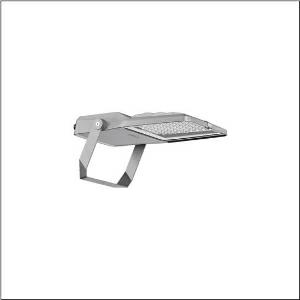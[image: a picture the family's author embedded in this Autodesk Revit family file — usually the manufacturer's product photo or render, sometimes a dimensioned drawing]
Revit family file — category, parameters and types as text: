
# Revit family: floodlight_fl_21_mini___pl61_5xa7772b1c1a_9d64
name_source: partatom
category: Lighting Fixtures
units: mm (PartAtom-declared; Revit-internal decimal feet)

## family parameters
Cut with Voids When Loaded = No
Host = Face
Light Source = No
Part Type = Normal
Room Calculation Point = No
Round Connector Dimension = Use Diameter
Shared = No

## types (1)
- --- (1 x LED, 5080 lm, 45.5 W, 2200K)
    Apparent Load = 46 VA
    CIE Flux Codes = 33 65 98 100 100
    Color Rendering = 70
    Color Temperature = 2200K
    Default Elevation = 1800 mm
    Description = Floodlight FL 21 mini, floodlight, primary light control with lens, of PMMA, primary optical cover: protective disc, of toughened safety glass, transparent, light distribution: PL61, light emission: direct distribution, installation type: surface-mounted, LED, High Power LED, rated luminous flux: 5.080lm, luminous efficacy: 112lm/W, light colour: 722, colour temperature: 2200K, control gear: ECG iQ, control: Street-Remote, Auto-Match, Temp-Guard, Night-Set, Smart-Wire, Desk-Remote (wireless, voltage-free reading and setting of iQ features in the workshop via application-optimized NFC function/RFID function), optimised constant luminous flux control (CLO 2.0), with terminal, 6-pole, mains connection: 220..240V, AC, 50/60Hz, start of lifetime: 46W, end of lifetime: 48W, reduction: 21W, luminaire housing, of diecast aluminium, powder-coated, Siteco® metallic grey (DB 702S), corrosivity category C5 according to DIN EN ISO 12944, mounting bracket, of steel, galvanised, powder-coated, Siteco® metallic grey (DB 702S), protection rating (complete): IP66, insulation class (complete): insulation class II (safety insulation), certification: CE, ENEC, VDE, protection symbol: D, impact resistance: IK08, permissible operating ambient temperature: -40..+40°C, permissible operating ambient temperature for outdoor applications: -40..+50°C, standard: DIN EN 12944, packaging unit: 1 piece

Light Distribution: PL61
    Height = 70 mm
    Lamp = 1 x LED
    Lamp Light Flux = 5080 lm
    Lamp Power = 45.5 W
    Lamp count = 1
    Length = 485 mm
    Luminous efficacy = 112 lm/W
    Manufacturer = Siteco
    ModVariant = No
    Model = 5XA7772B1C1A
    Number of Poles = 1
    OnlyDefault = Yes
    Power Factor = 1
    Product Name = Floodlight FL 21 mini | PL61
    Product group = floodlight | pylon top
    ProductGroupID = 6101
    Protection Class = Protection class II
    Protection Degree = IP 66
    RLX_Detail_Level = 1
    RlxData = <blob elided: 96057 chars, md5=0de16881>
    Socket = socket
    Standby Power = 0 W
    System Light Flux = 5080 lm
    System Power = 46 W
    Type Comments = factory setting: luminous flux: 100 % | dim-lin: 254 | 463 mA
    Type Image = l_1006845.jpg
    URL = http://relux.com
    VarID = @adj_086017
    Voltage = 0 V
    Weight = 0.00 kg
    Width = 337 mm

## geometry (parser evidence)
native form markers: Blend x4, Sweep x12
no freeform markers — native parametric forms only
